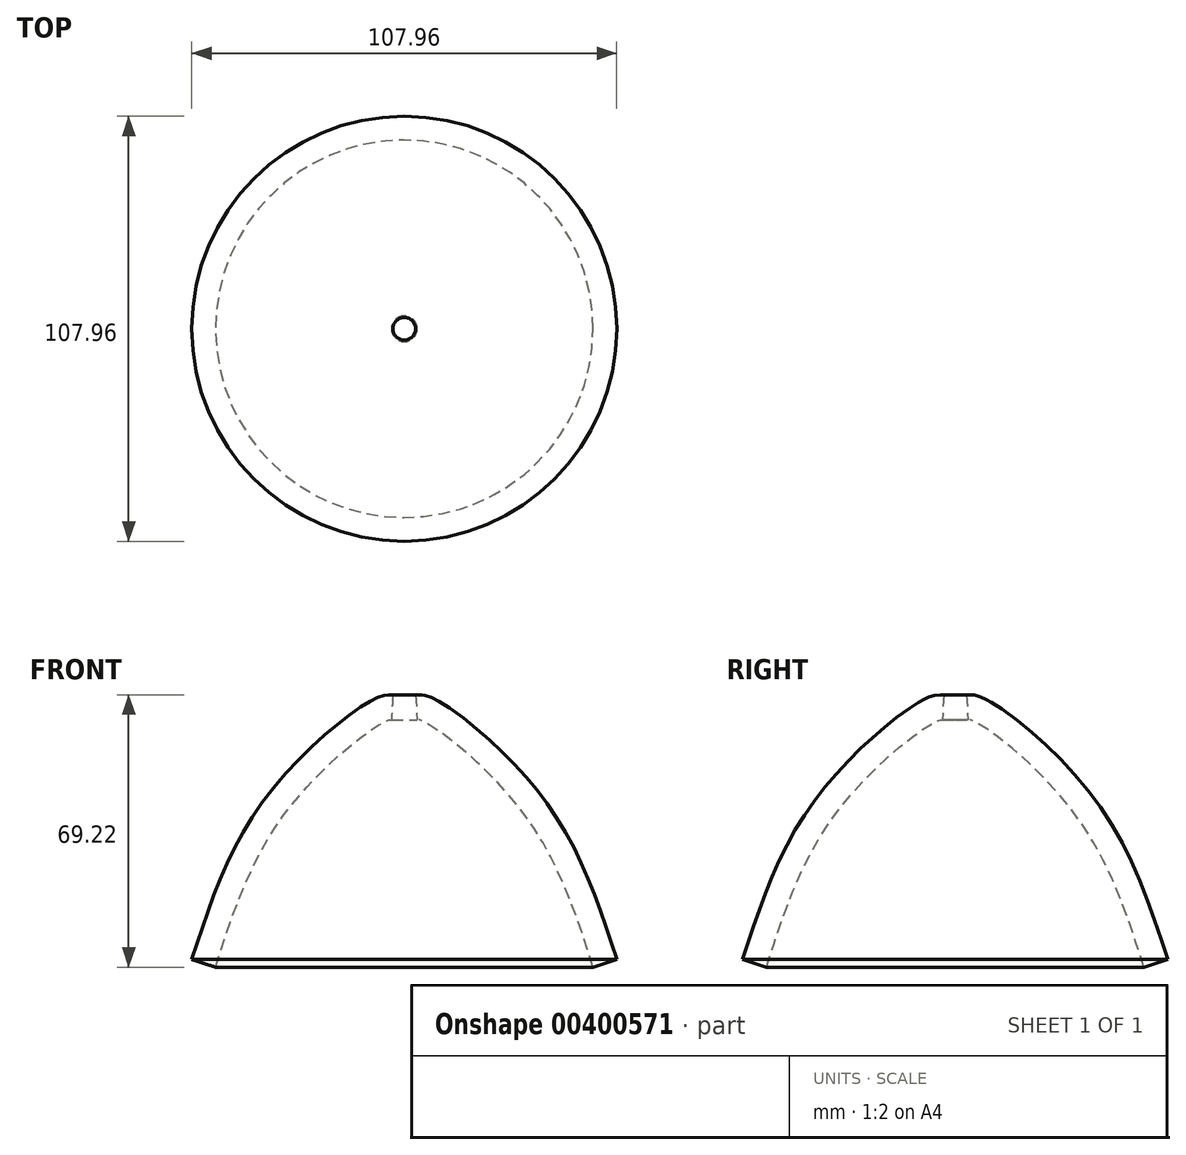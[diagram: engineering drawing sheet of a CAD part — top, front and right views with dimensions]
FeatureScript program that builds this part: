
annotation { "Feature Type Name" : "Feature", "Feature Type Description" : "" }
export const myFeature = defineFeature(function(context is Context, id is Id, definition is map)
    precondition{}
    {
        {
            var Q0;
            Q0=qCreatedBy(makeId("Right.planeOp"),FACE);
            var sketch = newSketch(context, id + "F0", { "sketchPlane" : qUnion([Q0])});
            skFitSpline(sketch, "E0", {"points": [v(-53.98, 0) * mm, v(-34.94, 41.45) * mm, v(-6.99, 66.51) * mm, v(-2.9, 67.24) * mm], "startDerivative": vector(30.46, 94.35) * mm, "endDerivative": vector(23.9, -1.36) * mm});
            skFitSpline(sketch, "E1.0", {"points": [v(-47.94, -1.95) * mm, v(-46.67, 1.98) * mm, v(-44.8, 7.8) * mm, v(-42.02, 15.3) * mm, v(-39.73, 20.8) * mm, v(-37.16, 26.16) * mm, v(-34.72, 30.5) * mm, v(-32.55, 33.9) * mm, v(-30.8, 36.42) * mm, v(-28.92, 38.9) * mm, v(-26.89, 41.36) * mm, v(-24.75, 43.78) * mm, v(-21.78, 46.92) * mm, v(-17.97, 50.62) * mm, v(-14.23, 53.87) * mm, v(-11.43, 56.1) * mm, v(-9.47, 57.58) * mm, v(-7.68, 58.83) * mm, v(-6.39, 59.65) * mm, v(-5.51, 60.16) * mm, v(-4.95, 60.46) * mm, v(-4.5, 60.68) * mm, v(-4.18, 60.8) * mm, v(-3.98, 60.88) * mm, v(-3.87, 60.91) * mm, v(-3.83, 60.92) * mm, v(-3.83, 60.92) * mm, v(-3.8, 60.92) * mm, v(-3.5, 60.91) * mm, v(-3.25, 60.9) * mm]});
            skLineSegment(sketch, "E2", {"start": v(-3.25, 60.9) * mm, "end": v(-2.9, 67.24) * mm});
            skLineSegment(sketch, "E3", {"start": v(-53.98, 0) * mm, "end": v(-47.94, -1.95) * mm});
            skLineSegment(sketch, "E4", {"start": v(0, 0) * mm, "end": v(0, 73.26) * mm, "construction": true});
            skSolve(sketch);
        }
        {
            var Q0;
            Q0 = qSketchRegion(id + "F0", true);
            var Q1;
            Q1=sQuery(id+"F0.wireOp",EDGE,"E4");
            revolve(context, id + "F1", {"entities" : qUnion([Q0]), "axis" : qUnion([Q1]), "revolveType" : RevolveType.FULL});
        }
    });
